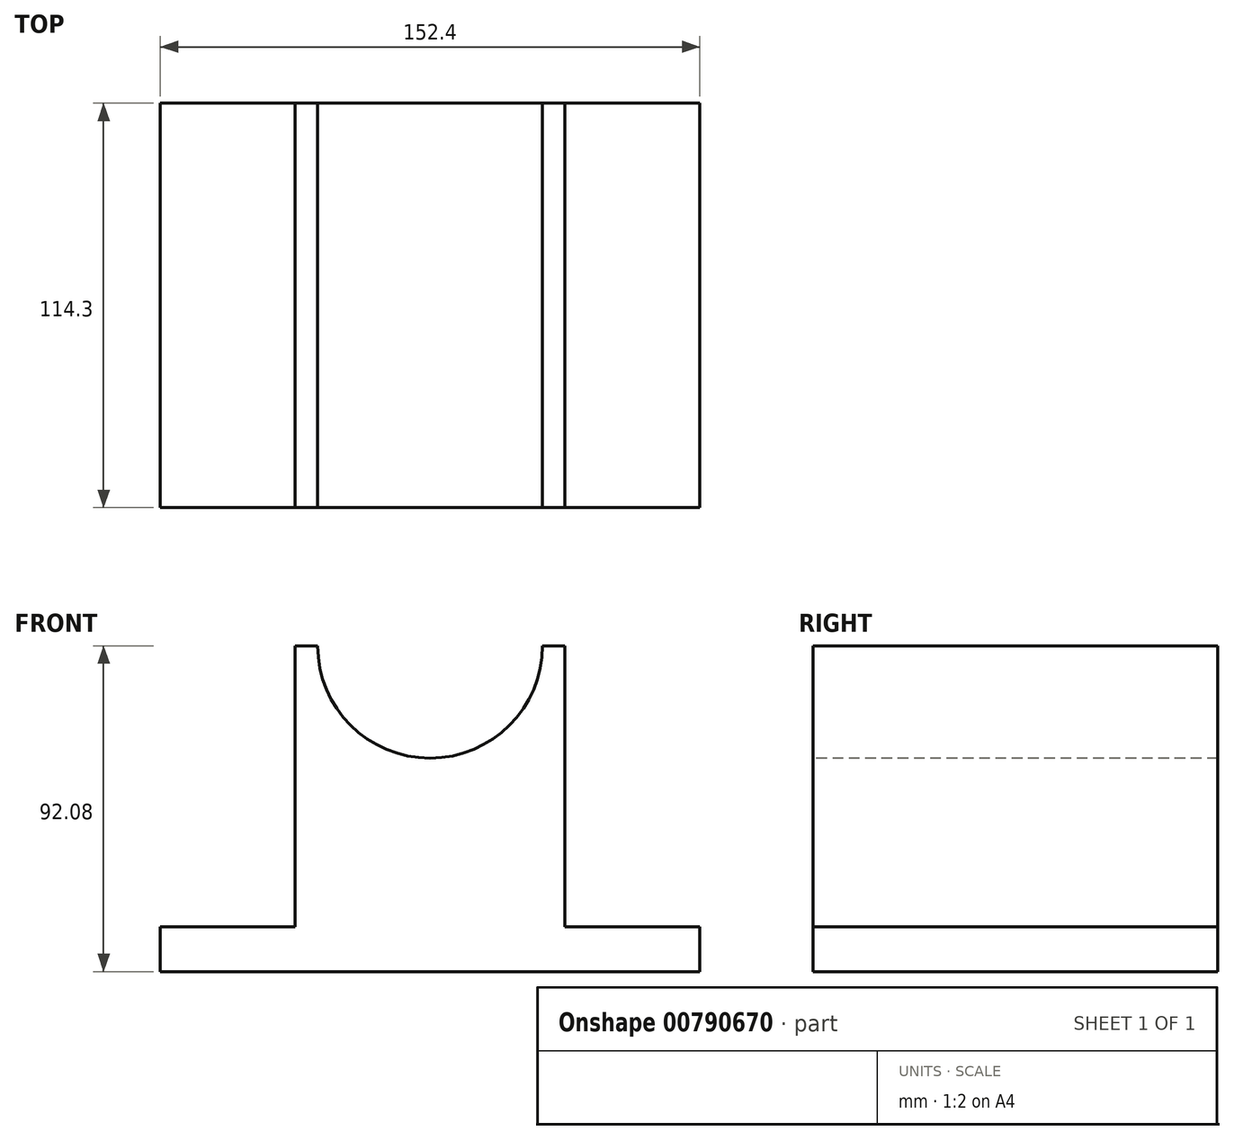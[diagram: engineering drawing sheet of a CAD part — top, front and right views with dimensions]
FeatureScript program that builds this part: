
annotation { "Feature Type Name" : "Feature", "Feature Type Description" : "" }
export const myFeature = defineFeature(function(context is Context, id is Id, definition is map)
    precondition{}
    {
        {
            var Q0;
            Q0=qCreatedBy(makeId("Front.planeOp"),FACE);
            var sketch = newSketch(context, id + "F0", { "sketchPlane" : qUnion([Q0])});
            skLineSegment(sketch, "E0", {"start": v(0, 0) * mm, "end": v(0, 12.7) * mm});
            skLineSegment(sketch, "E1", {"start": v(0, 12.7) * mm, "end": v(38.1, 12.7) * mm});
            skLineSegment(sketch, "E2", {"start": v(38.1, 12.7) * mm, "end": v(38.1, 92.08) * mm});
            skLineSegment(sketch, "E3", {"start": v(0, 0) * mm, "end": v(152.4, 0) * mm});
            skLineSegment(sketch, "E4", {"start": v(152.4, 0) * mm, "end": v(152.4, 12.7) * mm});
            skLineSegment(sketch, "E5", {"start": v(152.4, 12.7) * mm, "end": v(114.3, 12.7) * mm});
            skLineSegment(sketch, "E6", {"start": v(114.3, 12.7) * mm, "end": v(114.3, 92.08) * mm});
            skLineSegment(sketch, "E7", {"start": v(114.3, 92.08) * mm, "end": v(38.1, 92.08) * mm});
            skSolve(sketch);
        }
        {
            var Q0;
            Q0=makeQuery(id+"F0.imprint","IMPRINT",FACE,{"disambiguationData":[TD([[makeQuery(id+"F0.imprint","IMPRINT",EDGE,{"derivedFrom":sQuery(id+"F0.wireOp",EDGE,"E0")}),-1.0]])]});
            extrude(context, id + "F1", {"entities" : qUnion([Q0]), "depth" : 114.3 * mm, "offsetDistance" : 25.4 * mm});
        }
        {
            var Q0;
            Q0=makeQuery(id+"F1.opExtrude","CAP_FACE",FACE,{"disambiguationData":[OSD([sQuery(id+"F0.wireOp",EDGE,"E0"),sQuery(id+"F0.wireOp",EDGE,"E1"),sQuery(id+"F0.wireOp",EDGE,"E2"),sQuery(id+"F0.wireOp",EDGE,"E3"),sQuery(id+"F0.wireOp",EDGE,"E4"),sQuery(id+"F0.wireOp",EDGE,"E5"),sQuery(id+"F0.wireOp",EDGE,"E6"),sQuery(id+"F0.wireOp",EDGE,"E7")])],"isStart":false});
            var sketch = newSketch(context, id + "F2", { "sketchPlane" : qUnion([Q0])});
            skCircle(sketch, "E8", {"center": v(76.2, 92.08) * mm, "radius": 31.75 * mm});
            skSolve(sketch);
        }
        {
            var Q0;
            {var subQ0=sQuery(id+"F2.wireOp",EDGE,"E8");var subQ1=makeQuery(id+"F1.opExtrude","CAP_EDGE",EDGE,{"disambiguationData":[OSD([sQuery(id+"F0.wireOp",EDGE,"E7")])],"isStart":false});var subQ2=makeQuery(id+"F2.imprint","INTERSECT",VERTEX,{"disambiguationData":[OD(0.0)],"derivedFrom":[subQ1,subQ0]});Q0=makeQuery(id+"F2.imprint","IMPRINT",FACE,{"disambiguationData":[TD([[makeQuery(id+"F2.imprint","IMPRINT",EDGE,{"disambiguationData":[TD([[subQ2,-1.0]])],"derivedFrom":subQ0}),1.0]])]});}
            extrude(context, id + "F3", {"entities" : qUnion([Q0]), "operationType" : NewBodyOperationType.REMOVE, "oppositeDirection" : true, "depth" : 114.3 * mm, "offsetDistance" : 25.4 * mm});
        }
    });
